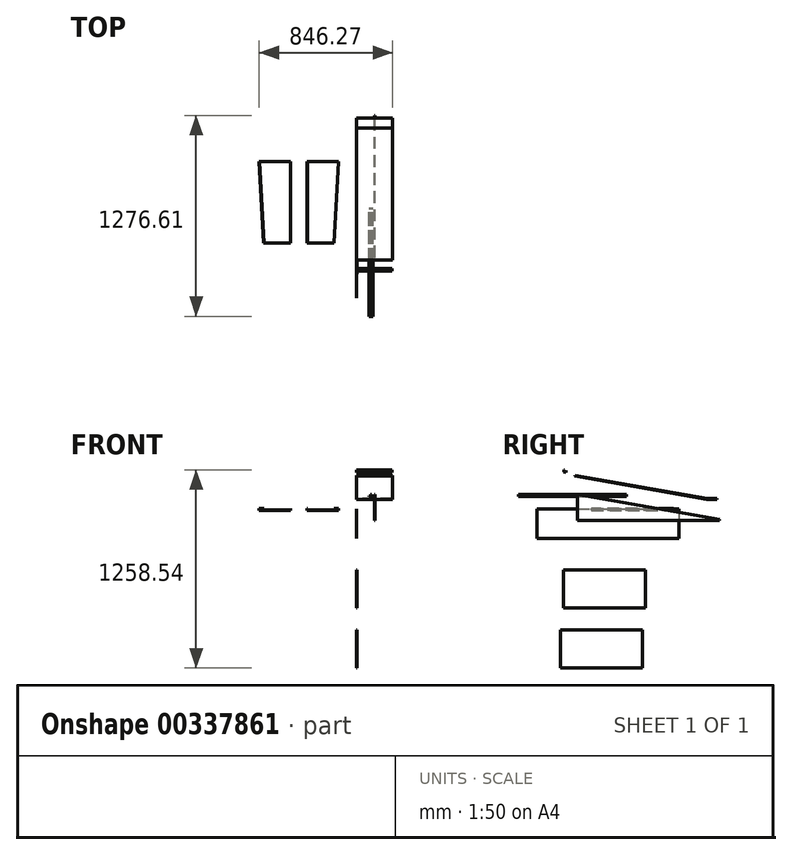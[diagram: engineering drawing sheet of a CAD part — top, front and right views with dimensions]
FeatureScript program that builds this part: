
annotation { "Feature Type Name" : "Feature", "Feature Type Description" : "" }
export const myFeature = defineFeature(function(context is Context, id is Id, definition is map)
    precondition{}
    {
        {
            var Q0;
            Q0=qCreatedBy(makeId("Right.planeOp"),FACE);
            var sketch = newSketch(context, id + "F0", { "sketchPlane" : qUnion([Q0])});
            skLineSegment(sketch, "E0.top", {"start": v(-310.9, -62.23) * mm, "end": v(590.8, -62.23) * mm});
            skLineSegment(sketch, "E0.left", {"start": v(-310.9, 103.12) * mm, "end": v(-310.9, -62.23) * mm});
            skLineSegment(sketch, "E1", {"start": v(590.8, -62.23) * mm, "end": v(590.8, -55.88) * mm});
            skLineSegment(sketch, "E2", {"start": v(-310.9, 103.12) * mm, "end": v(590.8, -55.88) * mm});
            skSolve(sketch);
        }
        {
            var Q0;
            Q0=makeQuery(id+"F0.imprint","IMPRINT",FACE,{"disambiguationData":[TD([[makeQuery(id+"F0.imprint","IMPRINT",EDGE,{"derivedFrom":sQuery(id+"F0.wireOp",EDGE,"E0.top")}),1.0]])]});
            extrude(context, id + "F1", {"entities" : qUnion([Q0]), "depth" : 116.84 * mm, "hasSecondDirection" : true, "secondDirectionOppositeDirection" : false, "secondDirectionDepth" : 115.25 * mm});
        }
        {
            var Q0;
            Q0=qCreatedBy(makeId("Right.planeOp"),FACE);
            var sketch = newSketch(context, id + "F2", { "sketchPlane" : qUnion([Q0])});
            skLineSegment(sketch, "E3", {"start": v(514.88, -36.04) * mm, "end": v(514.88, -34.45) * mm});
            skLineSegment(sketch, "E4.top", {"start": v(-327.65, 218.47) * mm, "end": v(510.56, 70.67) * mm});
            skLineSegment(sketch, "E5", {"start": v(510.56, 70.67) * mm, "end": v(574.06, 70.67) * mm});
            skLineSegment(sketch, "E6", {"start": v(574.06, 70.67) * mm, "end": v(574.06, 74.66) * mm});
            skLineSegment(sketch, "E7", {"start": v(574.06, 74.66) * mm, "end": v(510.9, 74.66) * mm});
            skLineSegment(sketch, "E8", {"start": v(-327.65, 222.52) * mm, "end": v(-327.65, 218.47) * mm});
            skLineSegment(sketch, "E9", {"start": v(510.9, 74.66) * mm, "end": v(-327.65, 222.52) * mm});
            skSolve(sketch);
        }
        {
            var Q0;
            Q0=qCreatedBy(makeId("Front.planeOp"),FACE);
            var sketch = newSketch(context, id + "F3", { "sketchPlane" : qUnion([Q0])});
            skLineSegment(sketch, "E10", {"start": v(93.93, 103.03) * mm, "end": v(93.93, 91.92) * mm});
            skLineSegment(sketch, "E11", {"start": v(93.93, 91.92) * mm, "end": v(105.04, 91.92) * mm});
            skLineSegment(sketch, "E12", {"start": v(105.04, 91.92) * mm, "end": v(105.04, 90.33) * mm});
            skLineSegment(sketch, "E13", {"start": v(105.04, 90.33) * mm, "end": v(92.34, 90.33) * mm});
            skLineSegment(sketch, "E14", {"start": v(92.34, 90.33) * mm, "end": v(92.34, 103.03) * mm});
            skLineSegment(sketch, "E15", {"start": v(92.34, 103.03) * mm, "end": v(93.93, 103.03) * mm});
            skLineSegment(sketch, "E16.MirrorCS", {"start": v(90.76, 90.33) * mm, "end": v(90.76, 103.03) * mm});
            skLineSegment(sketch, "E17.MirrorCS", {"start": v(89.17, 91.92) * mm, "end": v(78.06, 91.92) * mm});
            skLineSegment(sketch, "E18.MirrorCS", {"start": v(90.76, 103.03) * mm, "end": v(89.17, 103.03) * mm});
            skLineSegment(sketch, "E19.MirrorCS", {"start": v(89.17, 103.03) * mm, "end": v(89.17, 91.92) * mm});
            skLineSegment(sketch, "E20.MirrorCS", {"start": v(78.06, 91.92) * mm, "end": v(78.06, 90.33) * mm});
            skLineSegment(sketch, "E21.MirrorCS", {"start": v(78.06, 90.33) * mm, "end": v(90.76, 90.33) * mm});
            skSolve(sketch);
        }
        {
            var Q0;
            Q0 = qSketchRegion(id + "F3", true);
            extrude(context, id + "F4", {"entities" : qUnion([Q0]), "depth" : 685.8 * mm});
        }
        {
            var Q0;
            Q0 = qSketchRegion(id + "F2", true);
            extrude(context, id + "F5", {"entities" : qUnion([Q0]), "depth" : 228.6 * mm});
        }
        {
            var Q0;
            Q0=qCreatedBy(makeId("Right.planeOp"),FACE);
            var sketch = newSketch(context, id + "F6", { "sketchPlane" : qUnion([Q0])});
            skLineSegment(sketch, "E22", {"start": v(-395.16, 257.38) * mm, "end": v(-397.37, 244.87) * mm});
            skLineSegment(sketch, "E23", {"start": v(-397.37, 244.87) * mm, "end": v(-384.86, 242.67) * mm});
            skLineSegment(sketch, "E24", {"start": v(-384.86, 242.67) * mm, "end": v(-382.66, 255.18) * mm});
            skLineSegment(sketch, "E25", {"start": v(-395.16, 257.38) * mm, "end": v(-393.6, 257.1) * mm});
            skLineSegment(sketch, "E26", {"start": v(-393.6, 257.1) * mm, "end": v(-395.53, 246.16) * mm});
            skLineSegment(sketch, "E27", {"start": v(-395.53, 246.16) * mm, "end": v(-386.15, 244.5) * mm});
            skLineSegment(sketch, "E28", {"start": v(-386.15, 244.5) * mm, "end": v(-384.22, 255.45) * mm});
            skLineSegment(sketch, "E29", {"start": v(-384.22, 255.45) * mm, "end": v(-382.66, 255.18) * mm});
            skLineSegment(sketch, "E30.0", {"start": v(-395.16, 257.38) * mm, "end": v(-384.22, 255.45) * mm, "construction": true});
            skSolve(sketch);
        }
        {
            var Q0;
            Q0 = qSketchRegion(id + "F6", true);
            extrude(context, id + "F7", {"entities" : qUnion([Q0]), "depth" : 225.42 * mm});
        }
        {
            var Q0;
            Q0=qCreatedBy(makeId("Right.planeOp"),FACE);
            var sketch = newSketch(context, id + "F8", { "sketchPlane" : qUnion([Q0])});
            skLineSegment(sketch, "E31.bottom", {"start": v(-400.13, -378.5) * mm, "end": v(119.79, -378.5) * mm});
            skLineSegment(sketch, "E31.top", {"start": v(-400.13, -619.8) * mm, "end": v(119.79, -619.8) * mm});
            skLineSegment(sketch, "E31.left", {"start": v(-400.13, -378.5) * mm, "end": v(-400.13, -619.8) * mm});
            skLineSegment(sketch, "E31.right", {"start": v(119.79, -378.5) * mm, "end": v(119.79, -619.8) * mm});
            skSolve(sketch);
        }
        {
            var Q0;
            Q0=makeQuery(id+"F8.imprint","IMPRINT",FACE,{"disambiguationData":[TD([[makeQuery(id+"F8.imprint","IMPRINT",EDGE,{"derivedFrom":sQuery(id+"F8.wireOp",EDGE,"E31.bottom")}),-1.0]])]});
            extrude(context, id + "F9", {"entities" : qUnion([Q0]), "depth" : 4 * mm});
        }
        {
            var Q0;
            Q0=qCreatedBy(makeId("Right.planeOp"),FACE);
            var sketch = newSketch(context, id + "F10", { "sketchPlane" : qUnion([Q0])});
            skLineSegment(sketch, "E32.bottom", {"start": v(-417.36, -759.86) * mm, "end": v(103.34, -759.86) * mm});
            skLineSegment(sketch, "E32.top", {"start": v(-417.36, -1001.16) * mm, "end": v(103.34, -1001.16) * mm});
            skLineSegment(sketch, "E32.left", {"start": v(-417.36, -759.86) * mm, "end": v(-417.36, -1001.16) * mm});
            skLineSegment(sketch, "E32.right", {"start": v(103.34, -759.86) * mm, "end": v(103.34, -1001.16) * mm});
            skSolve(sketch);
        }
        {
            var Q0;
            Q0=makeQuery(id+"F10.imprint","IMPRINT",FACE,{"disambiguationData":[TD([[makeQuery(id+"F10.imprint","IMPRINT",EDGE,{"derivedFrom":sQuery(id+"F10.wireOp",EDGE,"E32.bottom")}),-1.0]])]});
            extrude(context, id + "F11", {"entities" : qUnion([Q0]), "depth" : 4 * mm});
        }
        {
            var Q0;
            Q0=qCreatedBy(makeId("Top.planeOp"),FACE);
            var sketch = newSketch(context, id + "F12", { "sketchPlane" : qUnion([Q0])});
            skLineSegment(sketch, "E33", {"start": v(-616.08, 298.97) * mm, "end": v(-587.5, -220.95) * mm});
            skLineSegment(sketch, "E34", {"start": v(-616.08, 298.97) * mm, "end": v(-419.23, 298.97) * mm});
            skLineSegment(sketch, "E35", {"start": v(-419.23, 298.97) * mm, "end": v(-419.23, -220.95) * mm});
            skLineSegment(sketch, "E36", {"start": v(-419.23, -220.95) * mm, "end": v(-587.5, -220.95) * mm});
            skLineSegment(sketch, "E37.MirrorCS", {"start": v(-311.44, -220.95) * mm, "end": v(-143.16, -220.95) * mm});
            skLineSegment(sketch, "E38.MirrorCS", {"start": v(-311.44, 298.97) * mm, "end": v(-311.44, -220.95) * mm});
            skLineSegment(sketch, "E39.MirrorCS", {"start": v(-114.59, 298.97) * mm, "end": v(-311.44, 298.97) * mm});
            skLineSegment(sketch, "E40.MirrorCS", {"start": v(-114.59, 298.97) * mm, "end": v(-143.16, -220.95) * mm});
            skSolve(sketch);
        }
        {
            var Q0;
            Q0 = qSketchRegion(id + "F12", true);
            extrude(context, id + "F13", {"entities" : qUnion([Q0]), "depth" : 1.59 * mm});
        }
        {
            var Q0;
            Q0=qCreatedBy(makeId("Top.planeOp"),FACE);
            var sketch = newSketch(context, id + "F14", { "sketchPlane" : qUnion([Q0])});
            skLineSegment(sketch, "E41", {"start": v(-616.09, 298.96) * mm, "end": v(-617.67, 298.96) * mm});
            skLineSegment(sketch, "E42", {"start": v(-616.09, 298.96) * mm, "end": v(-587.5, -220.95) * mm});
            skLineSegment(sketch, "E43", {"start": v(-587.5, -220.95) * mm, "end": v(-589.1, -220.95) * mm});
            skLineSegment(sketch, "E44", {"start": v(-589.1, -220.95) * mm, "end": v(-617.67, 298.96) * mm});
            skLineSegment(sketch, "E45", {"start": v(-419.23, 298.97) * mm, "end": v(-417.65, 298.97) * mm});
            skLineSegment(sketch, "E46", {"start": v(-419.23, -220.95) * mm, "end": v(-419.23, 298.97) * mm});
            skLineSegment(sketch, "E47", {"start": v(-419.23, -220.95) * mm, "end": v(-417.65, -220.95) * mm});
            skLineSegment(sketch, "E48", {"start": v(-417.65, -220.95) * mm, "end": v(-417.65, 298.97) * mm});
            skLineSegment(sketch, "E49.MirrorCS", {"start": v(-114.59, 298.96) * mm, "end": v(-113, 298.96) * mm});
            skLineSegment(sketch, "E50.MirrorCS", {"start": v(-311.44, 298.97) * mm, "end": v(-313.02, 298.97) * mm});
            skLineSegment(sketch, "E51.MirrorCS", {"start": v(-311.44, -220.95) * mm, "end": v(-313.02, -220.95) * mm});
            skLineSegment(sketch, "E52.MirrorCS", {"start": v(-143.16, -220.95) * mm, "end": v(-141.58, -220.95) * mm});
            skLineSegment(sketch, "E53.MirrorCS", {"start": v(-311.44, -220.95) * mm, "end": v(-311.44, 298.97) * mm});
            skLineSegment(sketch, "E54.MirrorCS", {"start": v(-114.59, 298.96) * mm, "end": v(-143.16, -220.95) * mm});
            skLineSegment(sketch, "E55.MirrorCS", {"start": v(-141.58, -220.95) * mm, "end": v(-113, 298.96) * mm});
            skLineSegment(sketch, "E56.MirrorCS", {"start": v(-313.02, -220.95) * mm, "end": v(-313.02, 298.97) * mm});
            skSolve(sketch);
        }
        {
            var Q0;
            Q0 = qSketchRegion(id + "F14", true);
            extrude(context, id + "F15", {"entities" : qUnion([Q0]), "operationType" : NewBodyOperationType.ADD, "depth" : 12.7 * mm});
        }
        {
            var Q0;
            Q0=qCreatedBy(makeId("Right.planeOp"),FACE);
            var sketch = newSketch(context, id + "F16", { "sketchPlane" : qUnion([Q0])});
            skLineSegment(sketch, "E57", {"start": v(-567.58, 8.04) * mm, "end": v(-567.58, -177.97) * mm});
            skLineSegment(sketch, "E58", {"start": v(-567.58, 8.04) * mm, "end": v(334.12, 8.04) * mm});
            skLineSegment(sketch, "E59", {"start": v(-567.58, -177.97) * mm, "end": v(334.12, -177.97) * mm});
            skLineSegment(sketch, "E60", {"start": v(334.12, 8.04) * mm, "end": v(334.12, -177.97) * mm});
            skSolve(sketch);
        }
        {
            var Q0;
            Q0=makeQuery(id+"F16.imprint","IMPRINT",FACE,{"disambiguationData":[TD([[makeQuery(id+"F16.imprint","IMPRINT",EDGE,{"derivedFrom":sQuery(id+"F16.wireOp",EDGE,"E57")}),1.0]])]});
            extrude(context, id + "F17", {"entities" : qUnion([Q0]), "depth" : 1.59 * mm});
        }
    });
